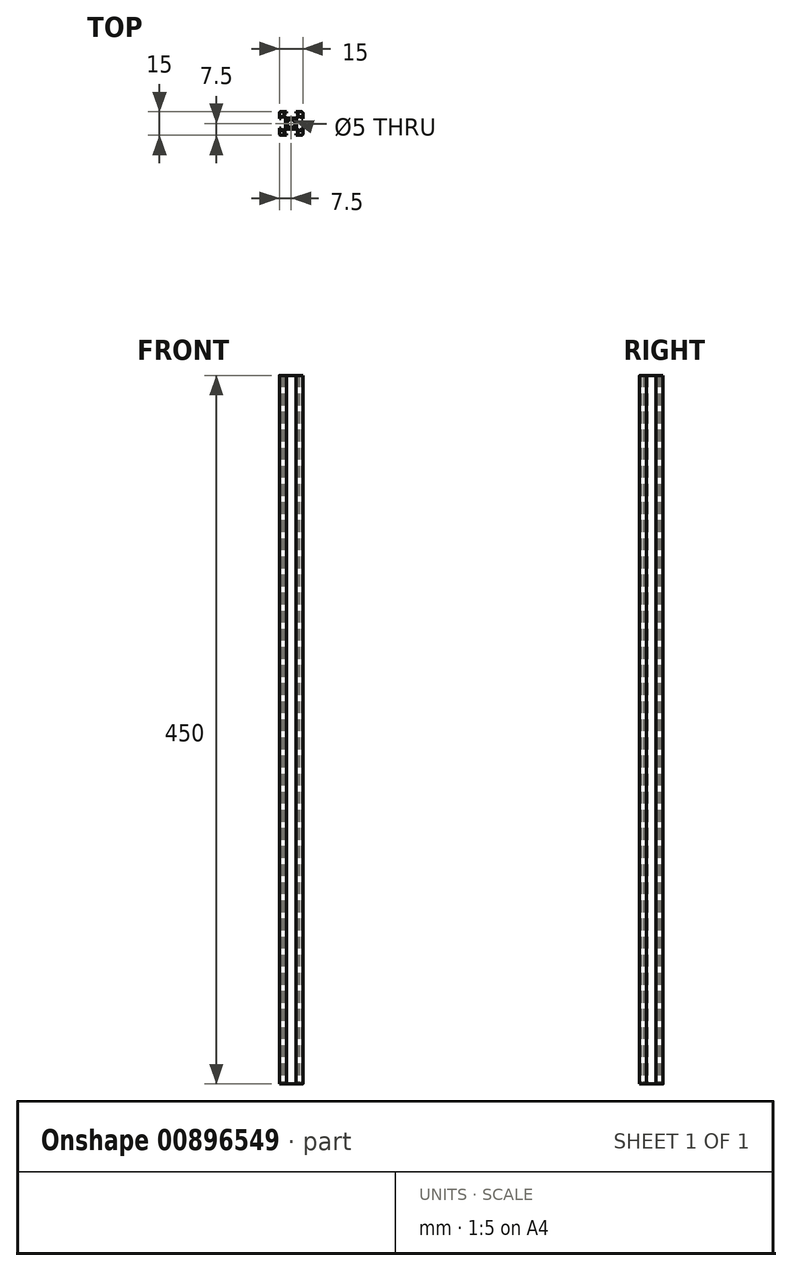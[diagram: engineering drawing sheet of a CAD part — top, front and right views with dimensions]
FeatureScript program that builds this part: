
annotation { "Feature Type Name" : "Feature", "Feature Type Description" : "" }
export const myFeature = defineFeature(function(context is Context, id is Id, definition is map)
    precondition{}
    {
        {
            assignVariable(context, id + "F0", {"name" : "height", "anyValue" : 450});
        }
        {
            var Q0;
            Q0=qCreatedBy(makeId("Top.planeOp"),FACE);
            var sketch = newSketch(context, id + "F1", { "sketchPlane" : qUnion([Q0])});
            skCircle(sketch, "E0", {"center": v(0, 0) * mm, "radius": 2.5 * mm});
            skLineSegment(sketch, "E1.bottom", {"start": v(6.5, 7.5) * mm, "end": v(3, 7.5) * mm});
            skLineSegment(sketch, "E1.top", {"start": v(6.5, -7.5) * mm, "end": v(3, -7.5) * mm});
            skLineSegment(sketch, "E1.left", {"start": v(7.5, 6.5) * mm, "end": v(7.5, 3) * mm});
            skLineSegment(sketch, "E1.right", {"start": v(-7.5, 6.5) * mm, "end": v(-7.5, 3) * mm});
            skPoint(sketch, "E2.visualSharp", {"position": v(-7.5, 7.5) * mm});
            skArc(sketch, "E2.filletArc", {"start": v(-6.5, 7.5) * mm, "mid": v(-7.2, 7.2) * mm, "end": v(-7.5, 6.5) * mm});
            skPoint(sketch, "E3.visualSharp", {"position": v(7.5, 7.5) * mm});
            skArc(sketch, "E3.filletArc", {"start": v(7.5, 6.5) * mm, "mid": v(7.2, 7.2) * mm, "end": v(6.5, 7.5) * mm});
            skPoint(sketch, "E4.visualSharp", {"position": v(7.5, -7.5) * mm});
            skArc(sketch, "E4.filletArc", {"start": v(6.5, -7.5) * mm, "mid": v(7.2, -7.2) * mm, "end": v(7.5, -6.5) * mm});
            skPoint(sketch, "E5.visualSharp", {"position": v(-7.5, -7.5) * mm});
            skArc(sketch, "E5.filletArc", {"start": v(-7.5, -6.5) * mm, "mid": v(-7.2, -7.2) * mm, "end": v(-6.5, -7.5) * mm});
            skLineSegment(sketch, "E6", {"start": v(-3, 7.5) * mm, "end": v(-3, 6.5) * mm});
            skLineSegment(sketch, "E7", {"start": v(3, 7.5) * mm, "end": v(3, 6.5) * mm});
            skLineSegment(sketch, "E8", {"start": v(-4.5, 6.5) * mm, "end": v(-4.5, 5) * mm});
            skLineSegment(sketch, "E9", {"start": v(4.5, 5) * mm, "end": v(4.5, 6.5) * mm});
            skLineSegment(sketch, "E10", {"start": v(4.5, 6.5) * mm, "end": v(3, 6.5) * mm});
            skLineSegment(sketch, "E11", {"start": v(-3, 3.5) * mm, "end": v(3, 3.5) * mm});
            skLineSegment(sketch, "E12", {"start": v(3, 3.5) * mm, "end": v(4.5, 5) * mm});
            skLineSegment(sketch, "E13", {"start": v(-3, 3.5) * mm, "end": v(-4.5, 5) * mm});
            skLineSegment(sketch, "E14.trimOffspring", {"start": v(-3, 6.5) * mm, "end": v(-4.5, 6.5) * mm});
            skLineSegment(sketch, "E15", {"start": v(-3, -7.5) * mm, "end": v(-3, -6.5) * mm});
            skLineSegment(sketch, "E16", {"start": v(-3, -6.5) * mm, "end": v(-4.5, -6.5) * mm});
            skLineSegment(sketch, "E17", {"start": v(-4.5, -6.5) * mm, "end": v(-4.5, -5) * mm});
            skLineSegment(sketch, "E18", {"start": v(-4.5, -5) * mm, "end": v(-3, -3.5) * mm});
            skLineSegment(sketch, "E19", {"start": v(-3, -3.5) * mm, "end": v(3, -3.5) * mm});
            skLineSegment(sketch, "E20", {"start": v(3, -3.5) * mm, "end": v(4.5, -5) * mm});
            skLineSegment(sketch, "E21", {"start": v(4.5, -5) * mm, "end": v(4.5, -6.5) * mm});
            skLineSegment(sketch, "E22", {"start": v(4.5, -6.5) * mm, "end": v(3, -6.5) * mm});
            skLineSegment(sketch, "E23", {"start": v(3, -6.5) * mm, "end": v(3, -7.5) * mm});
            skPoint(sketch, "E24", {"position": v(0, 7.5) * mm});
            skPoint(sketch, "E25", {"position": v(0, -7.5) * mm});
            skPoint(sketch, "E26", {"position": v(7.5, 0) * mm});
            skPoint(sketch, "E27", {"position": v(-7.5, 0) * mm});
            skLineSegment(sketch, "E28", {"start": v(7.5, 3) * mm, "end": v(6.5, 3) * mm});
            skLineSegment(sketch, "E29", {"start": v(6.5, 3) * mm, "end": v(6.5, 4.5) * mm});
            skLineSegment(sketch, "E30", {"start": v(6.5, 4.5) * mm, "end": v(5, 4.5) * mm});
            skLineSegment(sketch, "E31", {"start": v(5, 4.5) * mm, "end": v(3.5, 3) * mm});
            skLineSegment(sketch, "E32", {"start": v(3.5, 3) * mm, "end": v(3.5, -3) * mm});
            skLineSegment(sketch, "E33", {"start": v(3.5, -3) * mm, "end": v(5, -4.5) * mm});
            skLineSegment(sketch, "E34", {"start": v(5, -4.5) * mm, "end": v(6.5, -4.5) * mm});
            skLineSegment(sketch, "E35", {"start": v(6.5, -4.5) * mm, "end": v(6.5, -3) * mm});
            skLineSegment(sketch, "E36", {"start": v(6.5, -3) * mm, "end": v(7.5, -3) * mm});
            skLineSegment(sketch, "E37.trimOffspring", {"start": v(-3, 7.5) * mm, "end": v(-6.5, 7.5) * mm});
            skLineSegment(sketch, "E38.trimOffspring", {"start": v(7.5, -3) * mm, "end": v(7.5, -6.5) * mm});
            skLineSegment(sketch, "E39.trimOffspring", {"start": v(-3, -7.5) * mm, "end": v(-6.5, -7.5) * mm});
            skLineSegment(sketch, "E40", {"start": v(-7.5, 3) * mm, "end": v(-6.5, 3) * mm});
            skLineSegment(sketch, "E41", {"start": v(-6.5, 3) * mm, "end": v(-6.5, 4.5) * mm});
            skLineSegment(sketch, "E42", {"start": v(-6.5, 4.5) * mm, "end": v(-5, 4.5) * mm});
            skLineSegment(sketch, "E43", {"start": v(-5, 4.5) * mm, "end": v(-3.5, 3) * mm});
            skLineSegment(sketch, "E44", {"start": v(-3.5, 3) * mm, "end": v(-3.5, -3) * mm});
            skLineSegment(sketch, "E45", {"start": v(-3.5, -3) * mm, "end": v(-5, -4.5) * mm});
            skLineSegment(sketch, "E46", {"start": v(-5, -4.5) * mm, "end": v(-6.5, -4.5) * mm});
            skLineSegment(sketch, "E47", {"start": v(-6.5, -4.5) * mm, "end": v(-6.5, -3) * mm});
            skLineSegment(sketch, "E48", {"start": v(-6.5, -3) * mm, "end": v(-7.5, -3) * mm});
            skLineSegment(sketch, "E49.trimOffspring", {"start": v(-7.5, -3) * mm, "end": v(-7.5, -6.5) * mm});
            skSolve(sketch);
        }
        {
            var Q0;
            Q0=qSketchRegion(id+"F1",true);
            extrude(context, id + "F2", {"entities" : qUnion([Q0]), "depth" : (getVariable(context, 'height')) * mm, "offsetDistance" : 25 * mm});
        }
    });
